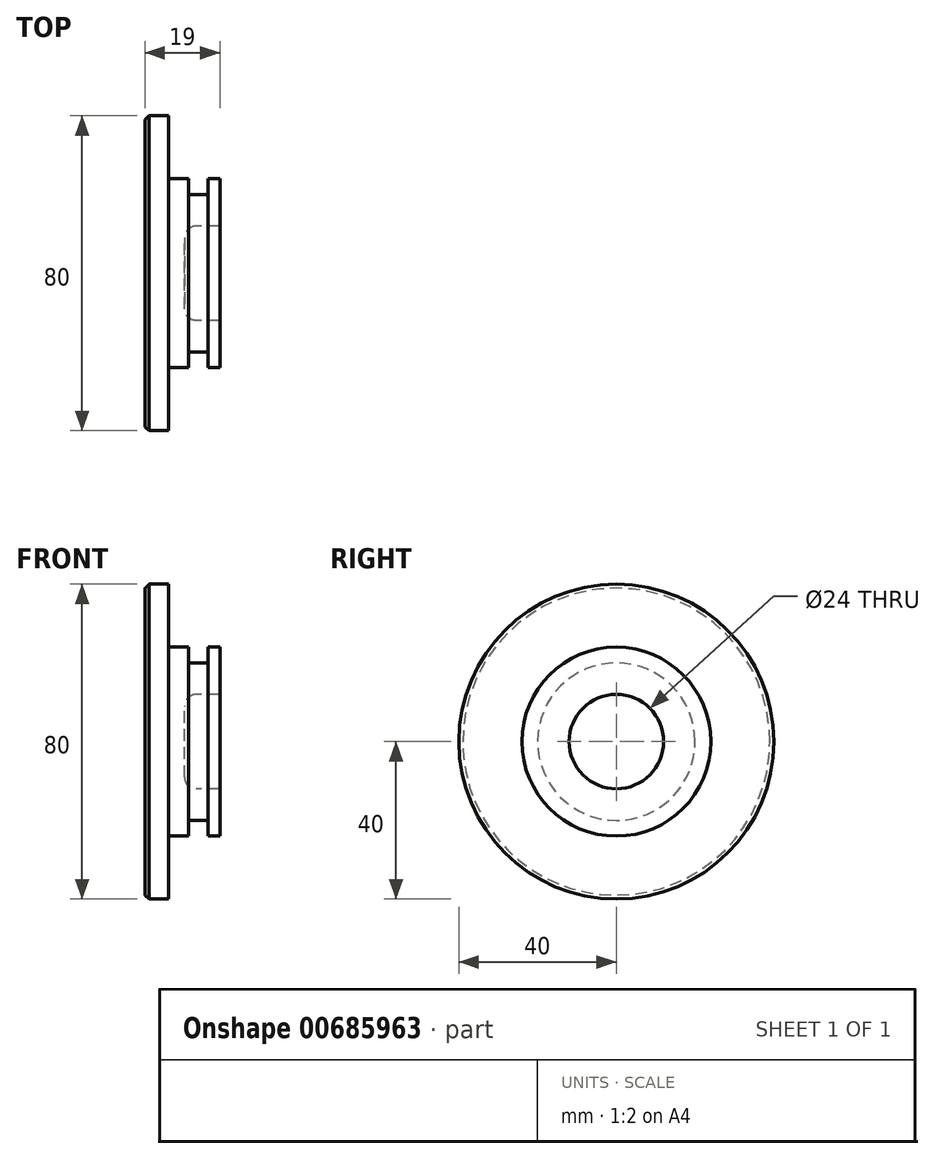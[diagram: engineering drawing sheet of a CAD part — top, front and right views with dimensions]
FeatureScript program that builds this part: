
annotation { "Feature Type Name" : "Feature", "Feature Type Description" : "" }
export const myFeature = defineFeature(function(context is Context, id is Id, definition is map)
    precondition{}
    {
        {
            var Q0;
            Q0=qCreatedBy(makeId("Front.planeOp"),FACE);
            var sketch = newSketch(context, id + "F0", { "sketchPlane" : qUnion([Q0])});
            skLineSegment(sketch, "E0", {"start": v(0, 0) * mm, "end": v(19, 0) * mm, "construction": true});
            skLineSegment(sketch, "E1", {"start": v(0, 0) * mm, "end": v(0, 40) * mm});
            skLineSegment(sketch, "E2", {"start": v(0, 40) * mm, "end": v(6, 40) * mm});
            skLineSegment(sketch, "E3", {"start": v(19, 12) * mm, "end": v(19, 24) * mm});
            skLineSegment(sketch, "E4", {"start": v(19, 24) * mm, "end": v(16, 24) * mm});
            skLineSegment(sketch, "E5", {"start": v(6, 24) * mm, "end": v(6, 40) * mm});
            skLineSegment(sketch, "E6", {"start": v(19, 12) * mm, "end": v(10, 12) * mm});
            skLineSegment(sketch, "E7", {"start": v(10, 12) * mm, "end": v(10, 0) * mm});
            skLineSegment(sketch, "E8", {"start": v(10, 0) * mm, "end": v(0, 0) * mm});
            skLineSegment(sketch, "E9", {"start": v(16, 24) * mm, "end": v(16, 20) * mm});
            skLineSegment(sketch, "E10", {"start": v(16, 20) * mm, "end": v(11, 20) * mm});
            skLineSegment(sketch, "E11", {"start": v(11, 20) * mm, "end": v(11, 24) * mm});
            skLineSegment(sketch, "E12.trimOffspring", {"start": v(11, 24) * mm, "end": v(6, 24) * mm});
            skSolve(sketch);
        }
        {
            var Q0;
            Q0 = qSketchRegion(id + "F0", true);
            var Q1;
            Q1=sQuery(id+"F0.wireOp",EDGE,"E0");
            revolve(context, id + "F1", {"entities" : qUnion([Q0]), "axis" : qUnion([Q1]), "revolveType" : RevolveType.FULL});
        }
        {
            var Q0;
            Q0=makeQuery(id+"F1.opRevolve","SWEPT_EDGE",EDGE,{"disambiguationData":[OSD([sQuery(id+"F0.wireOp",EDGE,"E1"),sQuery(id+"F0.wireOp",EDGE,"E2")])]});
            chamfer(context, id + "F2", {"entities" : qUnion([Q0]), "width" : 1 * mm, "tangentPropagation" : true});
        }
        {
            var Q0;
            Q0=makeQuery(id+"F1.opRevolve","SWEPT_EDGE",EDGE,{"disambiguationData":[OSD([sQuery(id+"F0.wireOp",EDGE,"E6"),sQuery(id+"F0.wireOp",EDGE,"E7")])]});
            fillet(context, id + "F3", {"entities" : qUnion([Q0]), "radius" : 3 * mm, "tangentPropagation" : true, "allowEdgeOverflow" : false});
        }
    });
